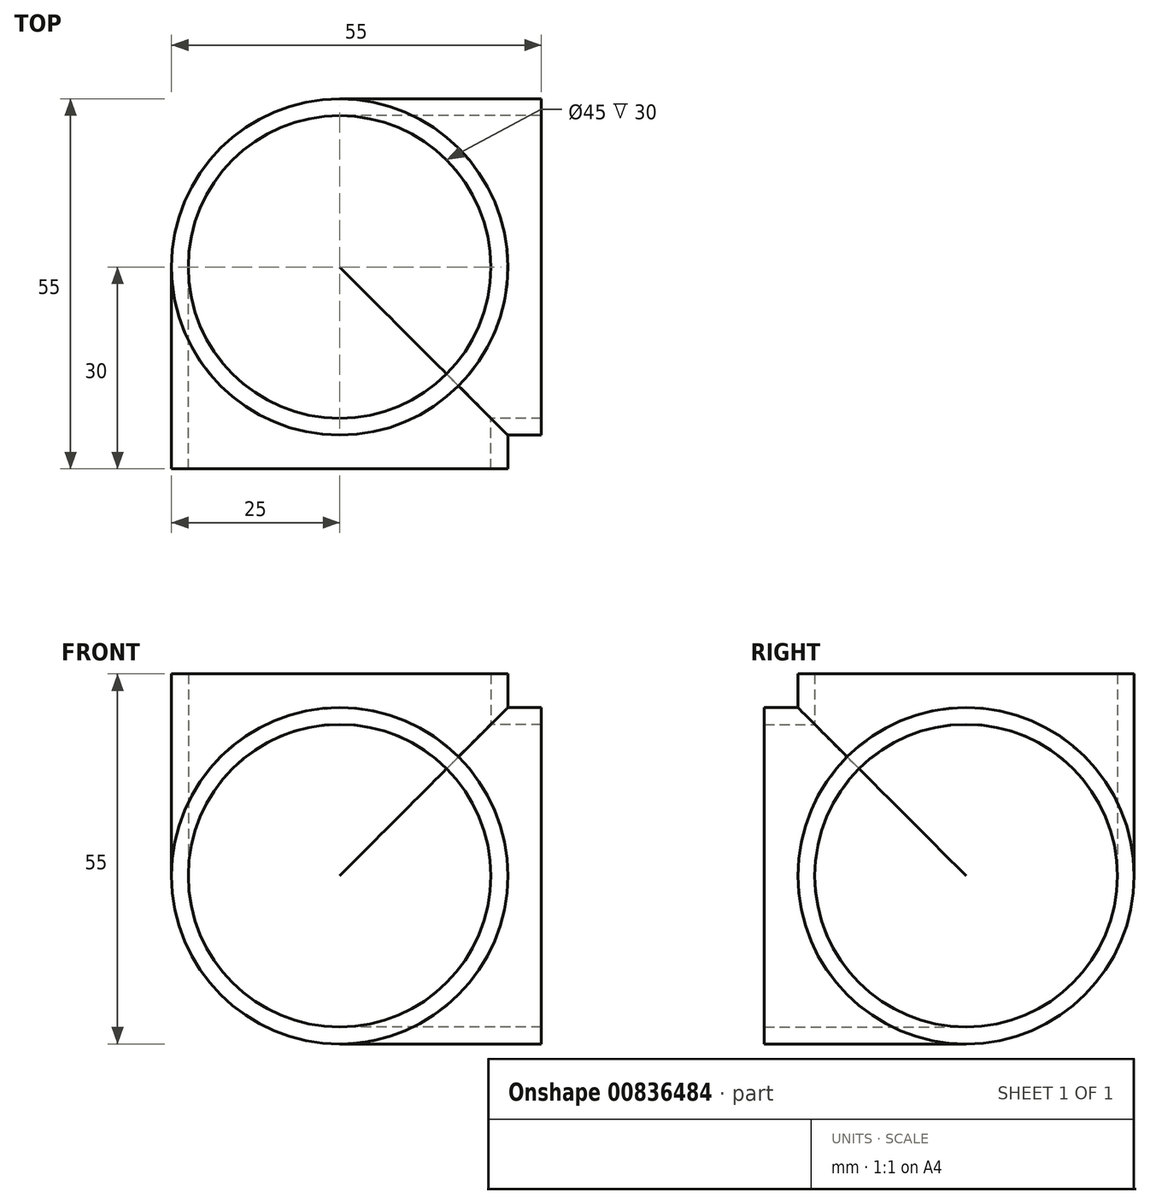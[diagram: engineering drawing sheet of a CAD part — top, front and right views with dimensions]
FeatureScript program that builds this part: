
annotation { "Feature Type Name" : "Feature", "Feature Type Description" : "" }
export const myFeature = defineFeature(function(context is Context, id is Id, definition is map)
    precondition{}
    {
        {
            var Q0;
            Q0=qCreatedBy(makeId("Front.planeOp"),FACE);
            var sketch = newSketch(context, id + "F0", { "sketchPlane" : qUnion([Q0])});
            skCircle(sketch, "E0", {"center": v(0, 0) * mm, "radius": 25 * mm});
            skSolve(sketch);
        }
        {
            var Q0;
            Q0=makeQuery(id+"F0.imprint","IMPRINT",FACE,{"disambiguationData":[TD([[makeQuery(id+"F0.imprint","IMPRINT",EDGE,{"derivedFrom":sQuery(id+"F0.wireOp",EDGE,"E0")}),1.0]])]});
            extrude(context, id + "F1", {"entities" : qUnion([Q0]), "depth" : 30 * mm, "offsetDistance" : 25 * mm});
        }
        {
            var Q0;
            Q0=qCreatedBy(makeId("Right.planeOp"),FACE);
            var sketch = newSketch(context, id + "F2", { "sketchPlane" : qUnion([Q0])});
            skCircle(sketch, "E1", {"center": v(0, 0) * mm, "radius": 25 * mm});
            skSolve(sketch);
        }
        {
            var Q0;
            Q0 = qSketchRegion(id + "F2", true);
            extrude(context, id + "F3", {"entities" : qUnion([Q0]), "operationType" : NewBodyOperationType.ADD, "depth" : 30 * mm, "offsetDistance" : 25 * mm});
        }
        {
            var Q0;
            Q0=qCreatedBy(makeId("Top.planeOp"),FACE);
            var sketch = newSketch(context, id + "F4", { "sketchPlane" : qUnion([Q0])});
            skCircle(sketch, "E2", {"center": v(0, 0) * mm, "radius": 25 * mm});
            skSolve(sketch);
        }
        {
            var Q0;
            Q0 = qSketchRegion(id + "F4", true);
            extrude(context, id + "F5", {"entities" : qUnion([Q0]), "operationType" : NewBodyOperationType.ADD, "depth" : 30 * mm, "offsetDistance" : 25 * mm});
        }
        {
            var Q0;
            Q0=makeQuery(id+"F3.opExtrude","CAP_FACE",FACE,{"disambiguationData":[OSD([sQuery(id+"F2.wireOp",EDGE,"E1")])],"isStart":true});
            var Q1;
            Q1=makeQuery(id+"F3.boolean.opBoolean","INTERSECT",EDGE,{"derivedFrom":[makeQuery(id+"F1.opExtrude","CAP_FACE",FACE,{"disambiguationData":[OSD([sQuery(id+"F0.wireOp",EDGE,"E0")])],"isStart":true}),makeQuery(id+"F3.opExtrude","CAP_FACE",FACE,{"disambiguationData":[OSD([sQuery(id+"F2.wireOp",EDGE,"E1")])],"isStart":true})]});
            revolve(context, id + "F6", {"operationType" : NewBodyOperationType.ADD, "surfaceOperationType" : NewSurfaceOperationType.NEW, "entities" : qUnion([Q0]), "axis" : qUnion([Q1]), "revolveType" : RevolveType.FULL});
        }
        {
            var Q0;
            Q0=makeQuery(id+"F1.opExtrude","CAP_FACE",FACE,{"disambiguationData":[OSD([sQuery(id+"F0.wireOp",EDGE,"E0")])],"isStart":false});
            var Q1;
            Q1=makeQuery(id+"F3.opExtrude","CAP_FACE",FACE,{"disambiguationData":[OSD([sQuery(id+"F2.wireOp",EDGE,"E1")])],"isStart":false});
            var Q2;
            Q2=makeQuery(id+"F5.opExtrude","CAP_FACE",FACE,{"disambiguationData":[OSD([sQuery(id+"F4.wireOp",EDGE,"E2")])],"isStart":false});
            shell(context, id + "F7", {"entities" : qUnion([Q0, Q1, Q2]), "thickness" : 2.5 * mm});
        }
    });
